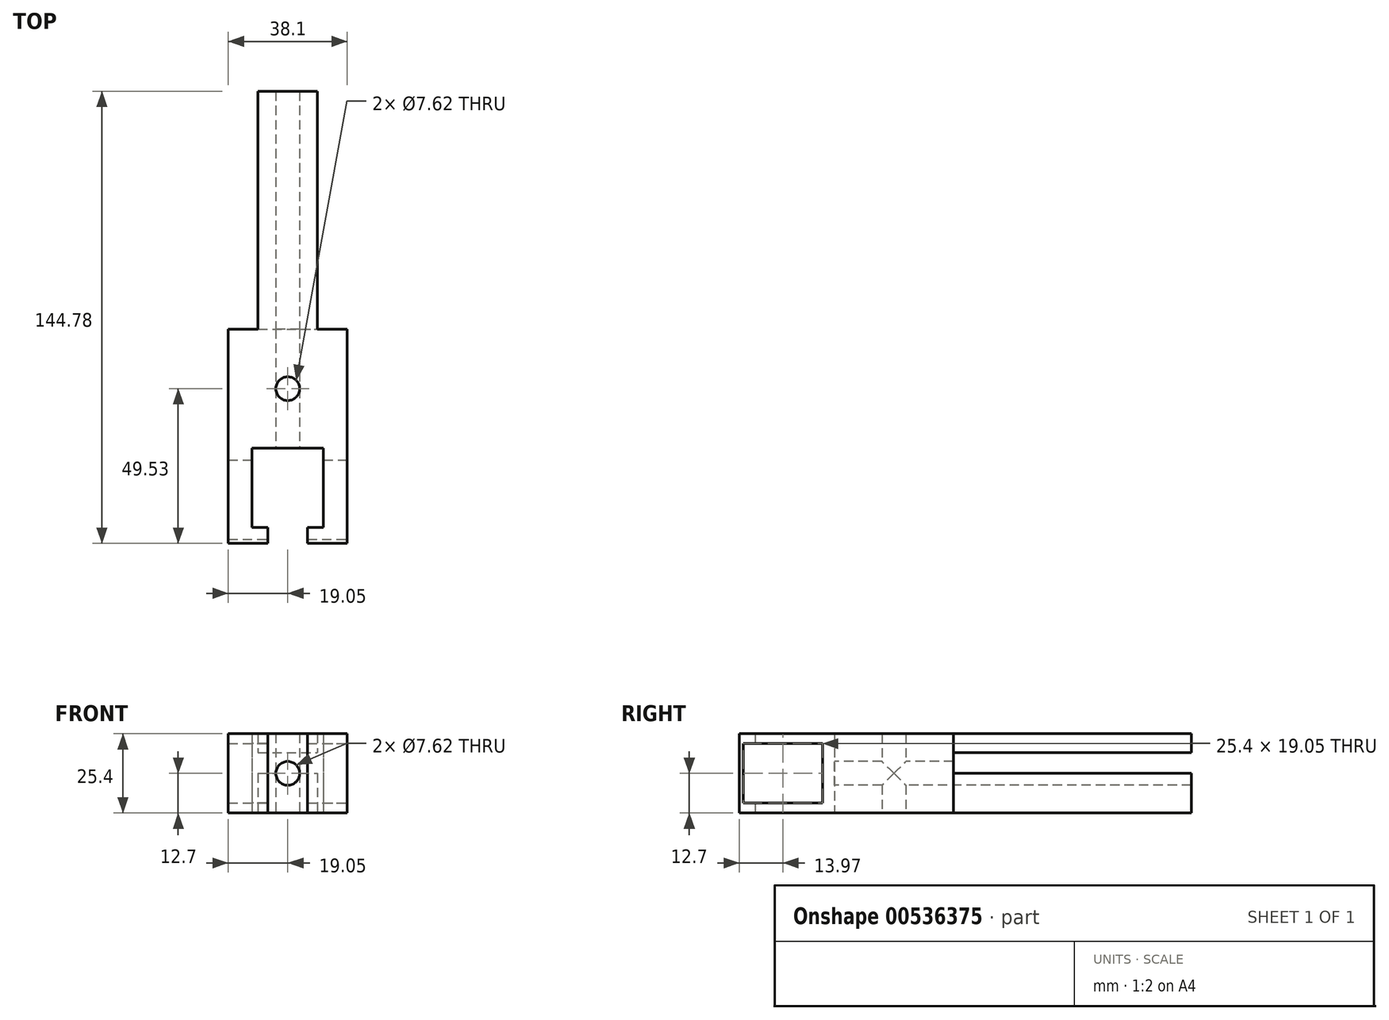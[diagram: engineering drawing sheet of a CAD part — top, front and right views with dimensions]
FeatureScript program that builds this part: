
annotation { "Feature Type Name" : "Feature", "Feature Type Description" : "" }
export const myFeature = defineFeature(function(context is Context, id is Id, definition is map)
    precondition{}
    {
        {
            var Q0;
            Q0=qCreatedBy(makeId("Top.planeOp"),FACE);
            var sketch = newSketch(context, id + "F0", { "sketchPlane" : qUnion([Q0])});
            skLineSegment(sketch, "E0.bottom", {"start": v(-19.05, 19.05) * mm, "end": v(19.05, 19.05) * mm});
            skLineSegment(sketch, "E0.top", {"start": v(-19.05, -19.05) * mm, "end": v(19.05, -19.05) * mm});
            skLineSegment(sketch, "E0.left", {"start": v(-19.05, 19.05) * mm, "end": v(-19.05, -19.05) * mm});
            skLineSegment(sketch, "E0.right", {"start": v(19.05, 19.05) * mm, "end": v(19.05, -19.05) * mm});
            skLineSegment(sketch, "E1.bottom", {"start": v(19.05, -19.05) * mm, "end": v(11.43, -19.05) * mm});
            skLineSegment(sketch, "E1.top", {"start": v(19.05, -49.53) * mm, "end": v(11.43, -49.53) * mm});
            skLineSegment(sketch, "E1.left", {"start": v(19.05, -19.05) * mm, "end": v(19.05, -49.53) * mm});
            skLineSegment(sketch, "E1.right", {"start": v(11.43, -19.05) * mm, "end": v(11.43, -49.53) * mm});
            skLineSegment(sketch, "E2.bottom", {"start": v(-19.05, -19.05) * mm, "end": v(-11.43, -19.05) * mm});
            skLineSegment(sketch, "E2.top", {"start": v(-19.05, -49.53) * mm, "end": v(-11.43, -49.53) * mm});
            skLineSegment(sketch, "E2.left", {"start": v(-19.05, -19.05) * mm, "end": v(-19.05, -49.53) * mm});
            skLineSegment(sketch, "E2.right", {"start": v(-11.43, -19.05) * mm, "end": v(-11.43, -49.53) * mm});
            skLineSegment(sketch, "E3.bottom", {"start": v(-19.05, -49.53) * mm, "end": v(-6.35, -49.53) * mm});
            skLineSegment(sketch, "E3.top", {"start": v(-19.05, -44.45) * mm, "end": v(-6.35, -44.45) * mm});
            skLineSegment(sketch, "E3.left", {"start": v(-19.05, -49.53) * mm, "end": v(-19.05, -44.45) * mm});
            skLineSegment(sketch, "E3.right", {"start": v(-6.35, -49.53) * mm, "end": v(-6.35, -44.45) * mm});
            skLineSegment(sketch, "E4.bottom", {"start": v(19.05, -49.53) * mm, "end": v(6.35, -49.53) * mm});
            skLineSegment(sketch, "E4.top", {"start": v(19.05, -44.45) * mm, "end": v(6.35, -44.45) * mm});
            skLineSegment(sketch, "E4.left", {"start": v(19.05, -49.53) * mm, "end": v(19.05, -44.45) * mm});
            skLineSegment(sketch, "E4.right", {"start": v(6.35, -49.53) * mm, "end": v(6.35, -44.45) * mm});
            skPoint(sketch, "E5", {"position": v(0, 19.05) * mm});
            skPoint(sketch, "E6", {"position": v(-19.05, 0) * mm});
            skCircle(sketch, "E7", {"center": v(0, 0) * mm, "radius": 3.81 * mm});
            skLineSegment(sketch, "E8", {"start": v(-19.05, 19.05) * mm, "end": v(0, 19.05) * mm});
            skPoint(sketch, "E9", {"position": v(-9.53, 19.05) * mm});
            skLineSegment(sketch, "E10", {"start": v(0, 19.05) * mm, "end": v(19.05, 19.05) * mm});
            skPoint(sketch, "E11", {"position": v(9.53, 19.05) * mm});
            skLineSegment(sketch, "E12.bottom", {"start": v(-9.53, 19.05) * mm, "end": v(9.52, 19.05) * mm});
            skLineSegment(sketch, "E12.top", {"start": v(-9.53, 95.25) * mm, "end": v(9.53, 95.25) * mm});
            skLineSegment(sketch, "E12.left", {"start": v(-9.53, 19.05) * mm, "end": v(-9.53, 95.25) * mm});
            skLineSegment(sketch, "E12.right", {"start": v(9.52, 19.05) * mm, "end": v(9.52, 95.25) * mm});
            skSolve(sketch);
        }
        {
            var Q0;
            Q0 = qSketchRegion(id + "F0", true);
            extrude(context, id + "F1", {"entities" : qUnion([Q0]), "depth" : 25.4 * mm, "offsetDistance" : 25.4 * mm});
        }
        {
            var Q0;
            Q0=makeQuery(id+"F1.opExtrude","SWEPT_FACE",FACE,{"disambiguationData":[OSD([sQuery(id+"F0.wireOp",EDGE,"E0.top")])]});
            var sketch = newSketch(context, id + "F2", { "sketchPlane" : qUnion([Q0])});
            skPoint(sketch, "E13", {"position": v(11.43, 12.7) * mm});
            skPoint(sketch, "E14", {"position": v(0, 12.7) * mm});
            skCircle(sketch, "E15", {"center": v(0, 12.7) * mm, "radius": 3.81 * mm});
            skSolve(sketch);
        }
        {
            var Q0;
            Q0=makeQuery(id+"F2.imprint","IMPRINT",FACE,{"disambiguationData":[TD([[makeQuery(id+"F2.imprint","IMPRINT",EDGE,{"derivedFrom":sQuery(id+"F2.wireOp",EDGE,"E15")}),1.0]])]});
            extrude(context, id + "F3", {"entities" : qUnion([Q0]), "operationType" : NewBodyOperationType.REMOVE, "endBound" : BoundingType.THROUGH_ALL, "oppositeDirection" : true, "depth" : 25.4 * mm, "offsetDistance" : 25.4 * mm});
        }
        {
            var Q0;
            Q0=makeQuery(id+"F1.opExtrude","SWEPT_FACE",FACE,{"disambiguationData":[OSD([sQuery(id+"F0.wireOp",EDGE,"E0.right"),sQuery(id+"F0.wireOp",EDGE,"E1.left"),sQuery(id+"F0.wireOp",EDGE,"E4.left")])]});
            var sketch = newSketch(context, id + "F4", { "sketchPlane" : qUnion([Q0])});
            skLineSegment(sketch, "E16.bottom", {"start": v(-48.26, 22.23) * mm, "end": v(-22.86, 22.23) * mm});
            skLineSegment(sketch, "E16.top", {"start": v(-48.26, 3.18) * mm, "end": v(-22.86, 3.18) * mm});
            skLineSegment(sketch, "E16.left", {"start": v(-48.26, 22.23) * mm, "end": v(-48.26, 3.18) * mm});
            skLineSegment(sketch, "E16.right", {"start": v(-22.86, 22.23) * mm, "end": v(-22.86, 3.18) * mm});
            skPoint(sketch, "E17", {"position": v(-48.26, 12.7) * mm});
            skPoint(sketch, "E18", {"position": v(-49.53, 12.7) * mm});
            skPoint(sketch, "E18.positionSnap0", {"position": v(-49.53, 12.7) * mm});
            skSolve(sketch);
        }
        {
            var Q0;
            Q0=makeQuery(id+"F4.imprint","IMPRINT",FACE,{"disambiguationData":[TD([[makeQuery(id+"F4.imprint","IMPRINT",EDGE,{"derivedFrom":sQuery(id+"F4.wireOp",EDGE,"E16.bottom")}),-1.0]])]});
            extrude(context, id + "F5", {"entities" : qUnion([Q0]), "operationType" : NewBodyOperationType.REMOVE, "endBound" : BoundingType.THROUGH_ALL, "oppositeDirection" : true, "depth" : 25.4 * mm, "offsetDistance" : 25.4 * mm});
        }
        {
            var Q0;
            Q0=makeQuery(id+"F1.opExtrude","SWEPT_FACE",FACE,{"disambiguationData":[OSD([sQuery(id+"F0.wireOp",EDGE,"E12.right")])]});
            var sketch = newSketch(context, id + "F6", { "sketchPlane" : qUnion([Q0])});
            skLineSegment(sketch, "E19", {"start": v(19.05, 12.7) * mm, "end": v(95.25, 12.7) * mm});
            skLineSegment(sketch, "E20", {"start": v(19.05, 19.3) * mm, "end": v(95.25, 19.3) * mm});
            skSolve(sketch);
        }
        {
            var Q0;
            {var subQ0=sQuery(id+"F6.wireOp",EDGE,"E19");Q0=makeQuery(id+"F6.imprint","IMPRINT",FACE,{"disambiguationData":[TD([[makeQuery(id+"F6.imprint","IMPRINT",EDGE,{"derivedFrom":subQ0}),1.0]])]});}
            extrude(context, id + "F7", {"entities" : qUnion([Q0]), "operationType" : NewBodyOperationType.REMOVE, "endBound" : BoundingType.THROUGH_ALL, "oppositeDirection" : true, "depth" : 25.4 * mm, "offsetDistance" : 25.4 * mm});
        }
    });
